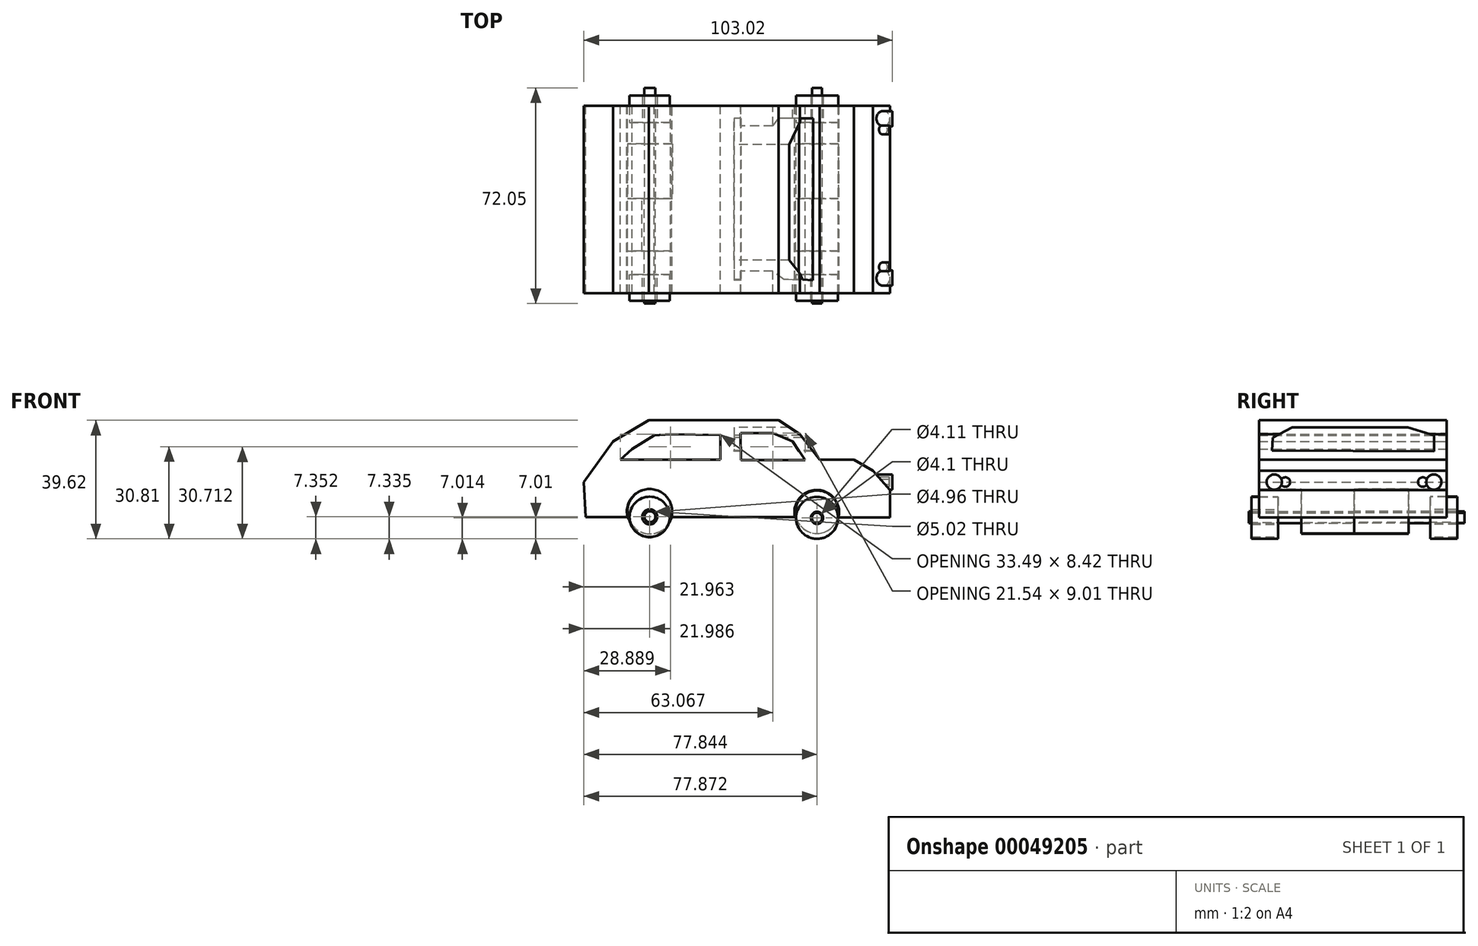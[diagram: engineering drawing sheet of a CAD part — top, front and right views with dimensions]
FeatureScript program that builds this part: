
annotation { "Feature Type Name" : "Feature", "Feature Type Description" : "" }
export const myFeature = defineFeature(function(context is Context, id is Id, definition is map)
    precondition{}
    {
        {
            var Q0;
            Q0=qCreatedBy(makeId("Front.planeOp"),FACE);
            var sketch = newSketch(context, id + "F0", { "sketchPlane" : qUnion([Q0])});
            skLineSegment(sketch, "E0", {"start": v(-50.14, 0) * mm, "end": v(-40.35, 13.61) * mm});
            skLineSegment(sketch, "E1", {"start": v(-40.35, 13.61) * mm, "end": v(-28.4, 20.66) * mm});
            skLineSegment(sketch, "E2", {"start": v(-28.4, 20.66) * mm, "end": v(14.89, 20.66) * mm});
            skLineSegment(sketch, "E3", {"start": v(14.89, 20.66) * mm, "end": v(21.94, 15.96) * mm});
            skLineSegment(sketch, "E4", {"start": v(21.94, 15.96) * mm, "end": v(28.6, 7.54) * mm});
            skLineSegment(sketch, "E5", {"start": v(28.6, 7.54) * mm, "end": v(39.96, 7.54) * mm});
            skLineSegment(sketch, "E6", {"start": v(39.96, 7.54) * mm, "end": v(46.42, 3.82) * mm});
            skLineSegment(sketch, "E7", {"start": v(46.42, 3.82) * mm, "end": v(52.1, -2.64) * mm});
            skLineSegment(sketch, "E8", {"start": v(52.1, -2.64) * mm, "end": v(52.1, -11.85) * mm});
            skLineSegment(sketch, "E9", {"start": v(52.1, -11.85) * mm, "end": v(34.86, -11.85) * mm});
            skLineSegment(sketch, "E10", {"start": v(20.32, -11.65) * mm, "end": v(-20.85, -11.65) * mm});
            skLineSegment(sketch, "E11", {"start": v(-49.55, -11.65) * mm, "end": v(-50.14, 0) * mm});
            skArc(sketch, "E12", {"start": v(-20.85, -11.65) * mm, "mid": v(-28.2, -2.33) * mm, "end": v(-35.56, -11.65) * mm});
            skArc(sketch, "E13", {"start": v(34.86, -11.85) * mm, "mid": v(27.72, -2.63) * mm, "end": v(20.32, -11.65) * mm});
            skLineSegment(sketch, "E14.trimOffspring", {"start": v(-35.56, -11.65) * mm, "end": v(-49.55, -11.65) * mm});
            skSolve(sketch);
        }
        {
            var Q0;
            Q0=makeQuery(id+"F0.imprint","IMPRINT",FACE,{"disambiguationData":[TD([[makeQuery(id+"F0.imprint","IMPRINT",EDGE,{"derivedFrom":sQuery(id+"F0.wireOp",EDGE,"E0")}),-1.0]])]});
            extrude(context, id + "F1", {"entities" : qUnion([Q0]), "depth" : 31.73 * mm});
        }
        {
            var Q0;
            Q0=makeQuery(id+"F0.imprint","IMPRINT",FACE,{"disambiguationData":[TD([[makeQuery(id+"F0.imprint","IMPRINT",EDGE,{"derivedFrom":sQuery(id+"F0.wireOp",EDGE,"E0")}),-1.0]])]});
            extrude(context, id + "F2", {"entities" : qUnion([Q0]), "operationType" : NewBodyOperationType.ADD, "oppositeDirection" : true, "depth" : 30.88 * mm});
        }
        {
            var Q0;
            Q0=qCreatedBy(makeId("Front.planeOp"),FACE);
            var sketch = newSketch(context, id + "F3", { "sketchPlane" : qUnion([Q0])});
            skLineSegment(sketch, "E15", {"start": v(2.15, 16.35) * mm, "end": v(12.93, 16.35) * mm});
            skLineSegment(sketch, "E16", {"start": v(12.93, 16.35) * mm, "end": v(19.59, 13.61) * mm});
            skLineSegment(sketch, "E17", {"start": v(19.59, 13.61) * mm, "end": v(23.7, 7.34) * mm});
            skLineSegment(sketch, "E18", {"start": v(23.7, 7.34) * mm, "end": v(2.35, 7.34) * mm});
            skLineSegment(sketch, "E19", {"start": v(2.35, 7.34) * mm, "end": v(2.15, 16.35) * mm});
            skLineSegment(sketch, "E20", {"start": v(-4.5, 15.77) * mm, "end": v(-4.5, 7.54) * mm});
            skLineSegment(sketch, "E21", {"start": v(-4.5, 7.54) * mm, "end": v(-21.15, 7.54) * mm});
            skLineSegment(sketch, "E22", {"start": v(-21.15, 15.96) * mm, "end": v(-4.5, 15.77) * mm});
            skLineSegment(sketch, "E23", {"start": v(-21.15, 7.54) * mm, "end": v(-38, 7.54) * mm});
            skLineSegment(sketch, "E24", {"start": v(-38, 7.54) * mm, "end": v(-34.08, 11.07) * mm});
            skLineSegment(sketch, "E25", {"start": v(-34.08, 11.07) * mm, "end": v(-26.64, 15.57) * mm});
            skLineSegment(sketch, "E26", {"start": v(-26.64, 15.57) * mm, "end": v(-21.15, 15.96) * mm});
            skSolve(sketch);
        }
        {
            var Q0;
            Q0 = qSketchRegion(id + "F3", true);
            extrude(context, id + "F4", {"entities" : qUnion([Q0]), "operationType" : NewBodyOperationType.REMOVE, "depth" : 105.3 * mm});
        }
        {
            var Q0;
            Q0=makeQuery(id+"F3.imprint","IMPRINT",FACE,{"disambiguationData":[TD([[makeQuery(id+"F3.imprint","IMPRINT",EDGE,{"derivedFrom":sQuery(id+"F3.wireOp",EDGE,"E15")}),-1.0]])]});
            var Q1;
            Q1=makeQuery(id+"F3.imprint","IMPRINT",FACE,{"disambiguationData":[TD([[makeQuery(id+"F3.imprint","IMPRINT",EDGE,{"derivedFrom":sQuery(id+"F3.wireOp",EDGE,"E20")}),-1.0]])]});
            extrude(context, id + "F5", {"entities" : qUnion([Q0, Q1]), "operationType" : NewBodyOperationType.REMOVE, "oppositeDirection" : true, "depth" : 57.13 * mm});
        }
        {
            var Q0;
            Q0=qCreatedBy(makeId("Right.planeOp"),FACE);
            var sketch = newSketch(context, id + "F6", { "sketchPlane" : qUnion([Q0])});
            skLineSegment(sketch, "E27", {"start": v(-20.61, 18.3) * mm, "end": v(18, 18.3) * mm});
            skLineSegment(sketch, "E28", {"start": v(18, 18.3) * mm, "end": v(26.7, 15.6) * mm});
            skLineSegment(sketch, "E29", {"start": v(26.7, 15.6) * mm, "end": v(26.7, 10.3) * mm});
            skLineSegment(sketch, "E30", {"start": v(26.7, 10.3) * mm, "end": v(-27.42, 10.48) * mm});
            skLineSegment(sketch, "E31", {"start": v(-20.61, 18.3) * mm, "end": v(-27.15, 14.84) * mm});
            skLineSegment(sketch, "E32", {"start": v(-27.15, 14.84) * mm, "end": v(-27.42, 10.48) * mm});
            skSolve(sketch);
        }
        {
            var Q0;
            Q0 = qSketchRegion(id + "F6", true);
            extrude(context, id + "F7", {"entities" : qUnion([Q0]), "operationType" : NewBodyOperationType.REMOVE, "depth" : 126.58 * mm});
        }
        {
            var Q0;
            Q0=qCreatedBy(makeId("Right.planeOp"),FACE);
            var sketch = newSketch(context, id + "F8", { "sketchPlane" : qUnion([Q0])});
            skCircle(sketch, "E33", {"center": v(-26.64, 0) * mm, "radius": 2.54 * mm});
            skCircle(sketch, "E34.MirrorC", {"center": v(26.64, 0) * mm, "radius": 2.54 * mm});
            skSolve(sketch);
        }
        {
            var Q0;
            Q0 = qSketchRegion(id + "F8", true);
            extrude(context, id + "F9", {"entities" : qUnion([Q0]), "operationType" : NewBodyOperationType.ADD, "depth" : 52.88 * mm});
        }
        {
            var Q0;
            Q0=qCreatedBy(makeId("Right.planeOp"),FACE);
            var sketch = newSketch(context, id + "F10", { "sketchPlane" : qUnion([Q0])});
            skCircle(sketch, "E35", {"center": v(-22.94, 0) * mm, "radius": 1.6 * mm});
            skCircle(sketch, "E36.MirrorC", {"center": v(22.94, 0) * mm, "radius": 1.6 * mm});
            skSolve(sketch);
        }
        {
            var Q0;
            Q0 = qSketchRegion(id + "F10", true);
            extrude(context, id + "F11", {"entities" : qUnion([Q0]), "operationType" : NewBodyOperationType.ADD, "depth" : 51.8 * mm});
        }
        {
            var Q0;
            Q0=qCreatedBy(makeId("Front.planeOp"),FACE);
            var sketch = newSketch(context, id + "F12", { "sketchPlane" : qUnion([Q0])});
            skCircle(sketch, "E37", {"center": v(27.7, -9.99) * mm, "radius": 7.17 * mm});
            skCircle(sketch, "E38", {"center": v(-28.09, -9.8) * mm, "radius": 7.5 * mm});
            skSolve(sketch);
        }
        {
            var Q0;
            Q0 = qSketchRegion(id + "F12", true);
            extrude(context, id + "F13", {"entities" : qUnion([Q0]), "operationType" : NewBodyOperationType.ADD, "depth" : 17.63 * mm});
        }
        {
            var Q0;
            Q0 = qSketchRegion(id + "F12", true);
            extrude(context, id + "F14", {"entities" : qUnion([Q0]), "oppositeDirection" : true, "depth" : 18.27 * mm});
        }
        {
            var Q0;
            Q0=qCreatedBy(makeId("Front.planeOp"),FACE);
            var sketch = newSketch(context, id + "F15", { "sketchPlane" : qUnion([Q0])});
            skCircle(sketch, "E39", {"center": v(27.7, -11.97) * mm, "radius": 1.7 * mm});
            skCircle(sketch, "E40", {"center": v(-28.09, -11.57) * mm, "radius": 1.84 * mm});
            skSolve(sketch);
        }
        {
            var Q0;
            Q0 = qSketchRegion(id + "F15", true);
            extrude(context, id + "F16", {"entities" : qUnion([Q0]), "depth" : 35.13 * mm});
        }
        {
            var Q0;
            Q0 = qSketchRegion(id + "F15", true);
            extrude(context, id + "F17", {"entities" : qUnion([Q0]), "oppositeDirection" : true, "depth" : 36.92 * mm});
        }
        {
            var Q0;
            Q0=qCreatedBy(makeId("Front.planeOp"),FACE);
            cPlane(context, id + "F18", {"entities" : qUnion([Q0]), "cplaneType" : CPlaneType.OFFSET, "offset" : 25.4 * mm, "width" : 152.4 * mm, "height" : 152.4 * mm});
        }
        {
            var Q0;
            Q0=qCreatedBy(makeId("Front.planeOp"),FACE);
            cPlane(context, id + "F19", {"entities" : qUnion([Q0]), "cplaneType" : CPlaneType.OFFSET, "offset" : 25.4 * mm, "oppositeDirection" : true, "width" : 152.4 * mm, "height" : 152.4 * mm});
        }
        {
            var Q0;
            Q0=qCreatedBy(id+"F18.planeOp",FACE);
            var sketch = newSketch(context, id + "F20", { "sketchPlane" : qUnion([Q0])});
            skCircle(sketch, "E41", {"center": v(-28.15, -11.6) * mm, "radius": 6.72 * mm});
            skCircle(sketch, "E42", {"center": v(-28.15, -11.6) * mm, "radius": 2.51 * mm});
            skCircle(sketch, "E43", {"center": v(27.7, -11.95) * mm, "radius": 2.05 * mm});
            skCircle(sketch, "E44", {"center": v(27.7, -11.95) * mm, "radius": 7 * mm});
            skSolve(sketch);
        }
        {
            var Q0;
            Q0 = qSketchRegion(id + "F20", true);
            extrude(context, id + "F21", {"entities" : qUnion([Q0]), "operationType" : NewBodyOperationType.ADD, "depth" : 8.78 * mm});
        }
        {
            var Q0;
            Q0=qCreatedBy(id+"F19.planeOp",FACE);
            var sketch = newSketch(context, id + "F22", { "sketchPlane" : qUnion([Q0])});
            skCircle(sketch, "E45", {"center": v(27.73, -11.95) * mm, "radius": 2.05 * mm});
            skCircle(sketch, "E46", {"center": v(27.73, -11.95) * mm, "radius": 7.01 * mm});
            skCircle(sketch, "E47", {"center": v(-28.18, -11.63) * mm, "radius": 2.48 * mm});
            skCircle(sketch, "E48", {"center": v(-28.18, -11.63) * mm, "radius": 6.77 * mm});
            skSolve(sketch);
        }
        {
            var Q0;
            Q0 = qSketchRegion(id + "F22", true);
            extrude(context, id + "F23", {"entities" : qUnion([Q0]), "oppositeDirection" : true, "depth" : 9.02 * mm});
        }
    });
